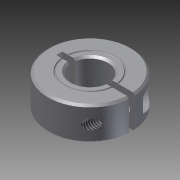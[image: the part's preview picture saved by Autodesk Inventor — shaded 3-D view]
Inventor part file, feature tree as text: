
AUTODESK INVENTOR PART (.ipt)
format: ipt  version: 2013 (Build 170138000, 138)  size: 368,640 bytes
history: native  units: mm
features: other x2, surface_op x1, thread x1
ambient origin geometry x8: Origin, YZ Plane, XZ Plane, XY Plane, X Axis, Y Axis, Z Axis, Center Point
bodies: Solid1 (feature_tree)
feature tree (4):
  surface_op  "Stitch Surface1"
  thread  "Thread1"  [1 undecoded]
  other  "Composite1"
  other  "Srf1"
note: 1 required parameter value undecoded (feature->parameter linkage not recoverable at this tier; creation-order binding heuristic only, values carry confidence <= 0.55)
